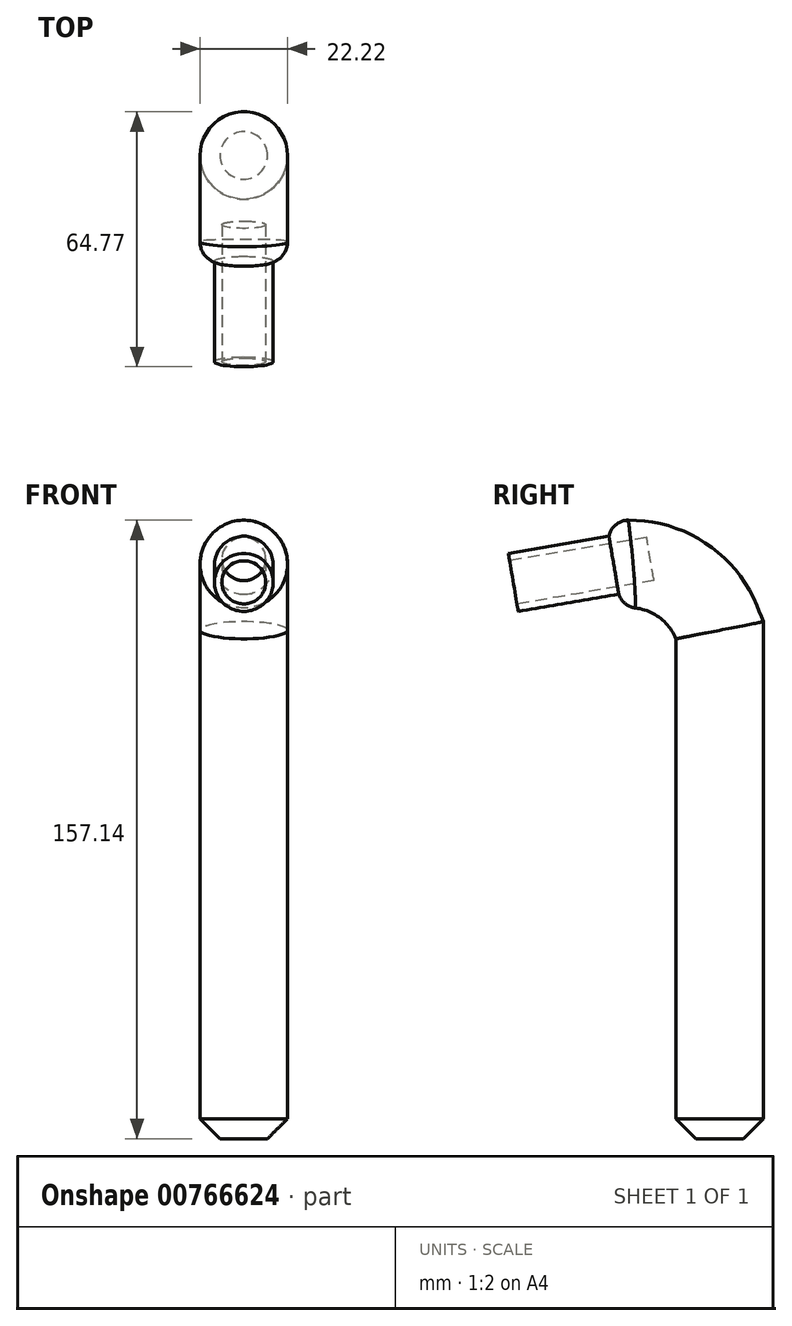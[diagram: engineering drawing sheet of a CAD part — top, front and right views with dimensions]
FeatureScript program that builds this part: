
annotation { "Feature Type Name" : "Feature", "Feature Type Description" : "" }
export const myFeature = defineFeature(function(context is Context, id is Id, definition is map)
    precondition{}
    {
        {
            var Q0;
            Q0=qCreatedBy(makeId("Right.planeOp"),FACE);
            var sketch = newSketch(context, id + "F0", { "sketchPlane" : qUnion([Q0])});
            skLineSegment(sketch, "E0", {"start": v(95.9, 0) * mm, "end": v(95.9, 127) * mm});
            skArc(sketch, "E1", {"start": v(95.9, 127) * mm, "mid": v(90.31, 133.31) * mm, "end": v(82, 134.74) * mm});
            skSolve(sketch);
        }
        {
            var Q0;
            Q0=qCreatedBy(makeId("Top.planeOp"),FACE);
            var sketch = newSketch(context, id + "F1", { "sketchPlane" : qUnion([Q0])});
            skCircle(sketch, "E2", {"center": v(0, 107.01) * mm, "radius": 11.11 * mm});
            skSolve(sketch);
        }
        {
            var Q0;
            Q0=makeQuery(id+"F1.imprint","IMPRINT",FACE,{"disambiguationData":[TD([[makeQuery(id+"F1.imprint","IMPRINT",EDGE,{"derivedFrom":sQuery(id+"F1.wireOp",EDGE,"E2")}),1.0]])]});
            var Q1;
            Q1=sQuery(id+"F0.wireOp",EDGE,"E1");
            var Q2;
            Q2=sQuery(id+"F0.wireOp",EDGE,"E0");
            sweep(context, id + "F2", {"profiles" : qUnion([Q0]), "path" : qUnion([Q1, Q2])});
        }
        {
            var Q0;
            Q0=makeQuery(id+"F2.opSweep","CAP_EDGE",EDGE,{"disambiguationData":[OSD([sQuery(id+"F0.wireOp",VERTEX,"E0.start"),sQuery(id+"F1.wireOp",EDGE,"E2")])],"isStart":true});
            chamfer(context, id + "F3", {"entities" : qUnion([Q0]), "width" : 5.08 * mm, "tangentPropagation" : true});
        }
        {
            var Q0;
            Q0=makeQuery(id+"F2.opSweep","CAP_FACE",FACE,{"disambiguationData":[OSD([sQuery(id+"F0.wireOp",VERTEX,"E1.end"),sQuery(id+"F1.wireOp",EDGE,"E2")])],"isStart":false});
            var sketch = newSketch(context, id + "F4", { "sketchPlane" : qUnion([Q0])});
            skCircle(sketch, "E3", {"center": v(0, 130.2) * mm, "radius": 7.48 * mm});
            skSolve(sketch);
        }
        {
            var Q0;
            Q0 = qSketchRegion(id + "F4", true);
            extrude(context, id + "F5", {"entities" : qUnion([Q0]), "operationType" : NewBodyOperationType.ADD, "depth" : 25.9 * mm, "offsetDistance" : 25.4 * mm});
        }
        {
            var Q0;
            Q0=makeQuery(id+"F2.opSweep","CAP_EDGE",EDGE,{"disambiguationData":[OSD([sQuery(id+"F0.wireOp",VERTEX,"E1.end"),sQuery(id+"F1.wireOp",EDGE,"E2")])],"isStart":false});
            fillet(context, id + "F6", {"entities" : qUnion([Q0]), "radius" : 5.08 * mm, "tangentPropagation" : true, "allowEdgeOverflow" : false});
        }
        {
            var Q0;
            Q0=makeQuery(id+"F5.opExtrude","CAP_FACE",FACE,{"disambiguationData":[OSD([sQuery(id+"F4.wireOp",EDGE,"E3")])],"isStart":false});
            var sketch = newSketch(context, id + "F7", { "sketchPlane" : qUnion([Q0])});
            skCircle(sketch, "E4", {"center": v(0, 130.2) * mm, "radius": 5.56 * mm});
            skSolve(sketch);
        }
        {
            var Q0;
            Q0 = qSketchRegion(id + "F7", true);
            extrude(context, id + "F8", {"entities" : qUnion([Q0]), "operationType" : NewBodyOperationType.REMOVE, "oppositeDirection" : true, "depth" : 35.3 * mm, "offsetDistance" : 25.4 * mm});
        }
    });
